# Revit family: QF_Vollrath_VCBF118-37
name_source: partatom
category: Specialty Equipment
revit_build: Autodesk Revit 2016 (Build: 20151007_0715(x64)
units: mm (PartAtom-declared; Revit-internal decimal feet)

## family parameters
Always vertical = Yes
Cut with Voids When Loaded = No
OmniClass Number = 23.40.40.00
OmniClass Title = Food Service Equipment and Furnishings
Part Type = Normal
Room Calculation Point = No
Round Connector Dimension = Use Diameter
Shared = No
Work Plane-Based = No

## types (1)
- QF_Vollrath_VCBF118-37
    Apparent Power = 552 VA
    Conn Plug = NEMA 5-15P
    Cycle = 60 Hz
    Depth = 20.32 "
    Description = Granita Countertop Dispenser
    Elec Conn Connection Height = 2 "
    FL Amps = 5 A
    Foodservice Equipment Identifier = Yes
    Height = 26.14 "
    Manufacturer = Vollrath
    Model = VCBF118-37
    Phase = 1
    URL = www.vollrath.com
    Volts = 115 V
    Weight in Pounds = 0
    Width = 7.64 "

## geometry (parser evidence)
native form markers: Sweep x7
no freeform markers — native parametric forms only
